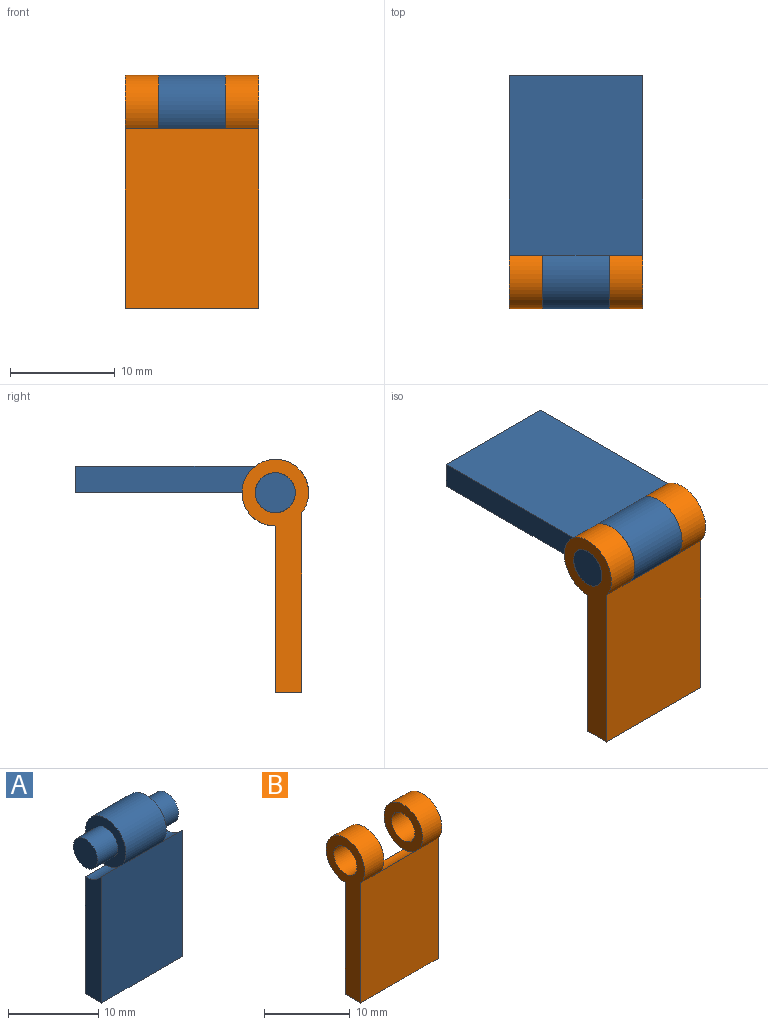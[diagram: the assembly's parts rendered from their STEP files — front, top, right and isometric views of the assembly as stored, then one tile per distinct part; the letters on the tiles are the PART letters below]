
ASSEMBLY  parts=2 mates=1
PART A: 14 faces, bbox 12.7x6.4x22.2 mm
  f0: plane 17.15x2.54mm, normal (-1,0,0), area 41.3mm2, adj f2,f3,f4,f10
  f1: cylinder r=3.17mm len=6.35mm, axis (-1,0,0), area 108mm2, adj f2,f4,f8,f12
  f2: plane 17.15x12.7mm, normal (0,-1,0), area 217.7mm2, adj f0,f1,f3,f5,f6,f10
  f3: plane 12.7x2.54mm, normal (0,0,-1), area 32.3mm2, adj f0,f2,f4,f5
  f4: plane 15.88x12.7mm, normal (0,1,0), area 201.6mm2, adj f0,f1,f3,f5,f6,f10
  f5: plane 17.15x2.54mm, normal (1,0,0), area 41.3mm2, adj f2,f3,f4,f6
  f6: cylinder r=3.17mm len=3.18mm, axis (1,0,0), area 9.3mm2, adj f2,f4,f5,f8
  f7: cylinder r=1.91mm len=3.81mm, axis (1,0,0), area 38mm2, adj f8,f9
  f8: plane 6.35x6.35mm, normal (1,0,0), area 20.3mm2, adj f1,f6,f7
  f9: plane 3.81x3.81mm, normal (1,0,0), area 11.4mm2, adj f7
  f10: cylinder r=3.17mm len=3.18mm, axis (-1,0,0), area 9.3mm2, adj f0,f2,f4,f12
  f11: cylinder r=1.91mm len=3.81mm, axis (-1,0,0), area 38mm2, adj f12,f13
  f12: plane 6.35x6.35mm, normal (-1,0,0), area 20.3mm2, adj f1,f10,f11
  f13: plane 3.81x3.81mm, normal (-1,0,0), area 11.4mm2, adj f11
PART B: 12 faces, bbox 12.7x6.4x22.2 mm
  f0: cylinder r=1.91mm len=3.81mm, axis (-1,0,0), area 38mm2, adj f8,f10
  f1: cylinder r=3.17mm len=6.35mm, axis (-1,0,0), area 54mm2, adj f2,f4,f8,f10
  f2: plane 17.15x12.7mm, normal (0,-1,0), area 217.7mm2, adj f1,f3,f6,f7,f8,f9
  f3: plane 12.7x2.54mm, normal (0,0,-1), area 32.3mm2, adj f2,f4,f7,f8
  f4: plane 15.88x12.7mm, normal (0,1,0), area 201.6mm2, adj f1,f3,f6,f7,f8,f9
  f5: cylinder r=1.91mm len=3.81mm, axis (-1,0,0), area 38mm2, adj f7,f11
  f6: cylinder r=3.17mm len=6.35mm, axis (-1,0,0), area 54mm2, adj f2,f4,f7,f11
  f7: plane 22.23x6.35mm, normal (1,0,0), area 61.6mm2, adj f2,f3,f4,f5,f6
  f8: plane 22.23x6.35mm, normal (-1,0,0), area 61.6mm2, adj f0,f1,f2,f3,f4
  f9: cylinder r=3.17mm len=6.35mm, axis (1,0,0), area 18.7mm2, adj f2,f4,f10,f11
  f10: plane 6.35x6.35mm, normal (1,0,0), area 20.3mm2, adj f0,f1,f9
  f11: plane 6.35x6.35mm, normal (-1,0,0), area 20.3mm2, adj f5,f6,f9
PLACE A rot(axis=(0,-0.71,0.71),180deg) t=(0,11.11,11.11)mm
PLACE B at identity
MATE revolute A.f7 <-> B.f0  axis (1,0,0) through (6.35,0,11.11)mm
